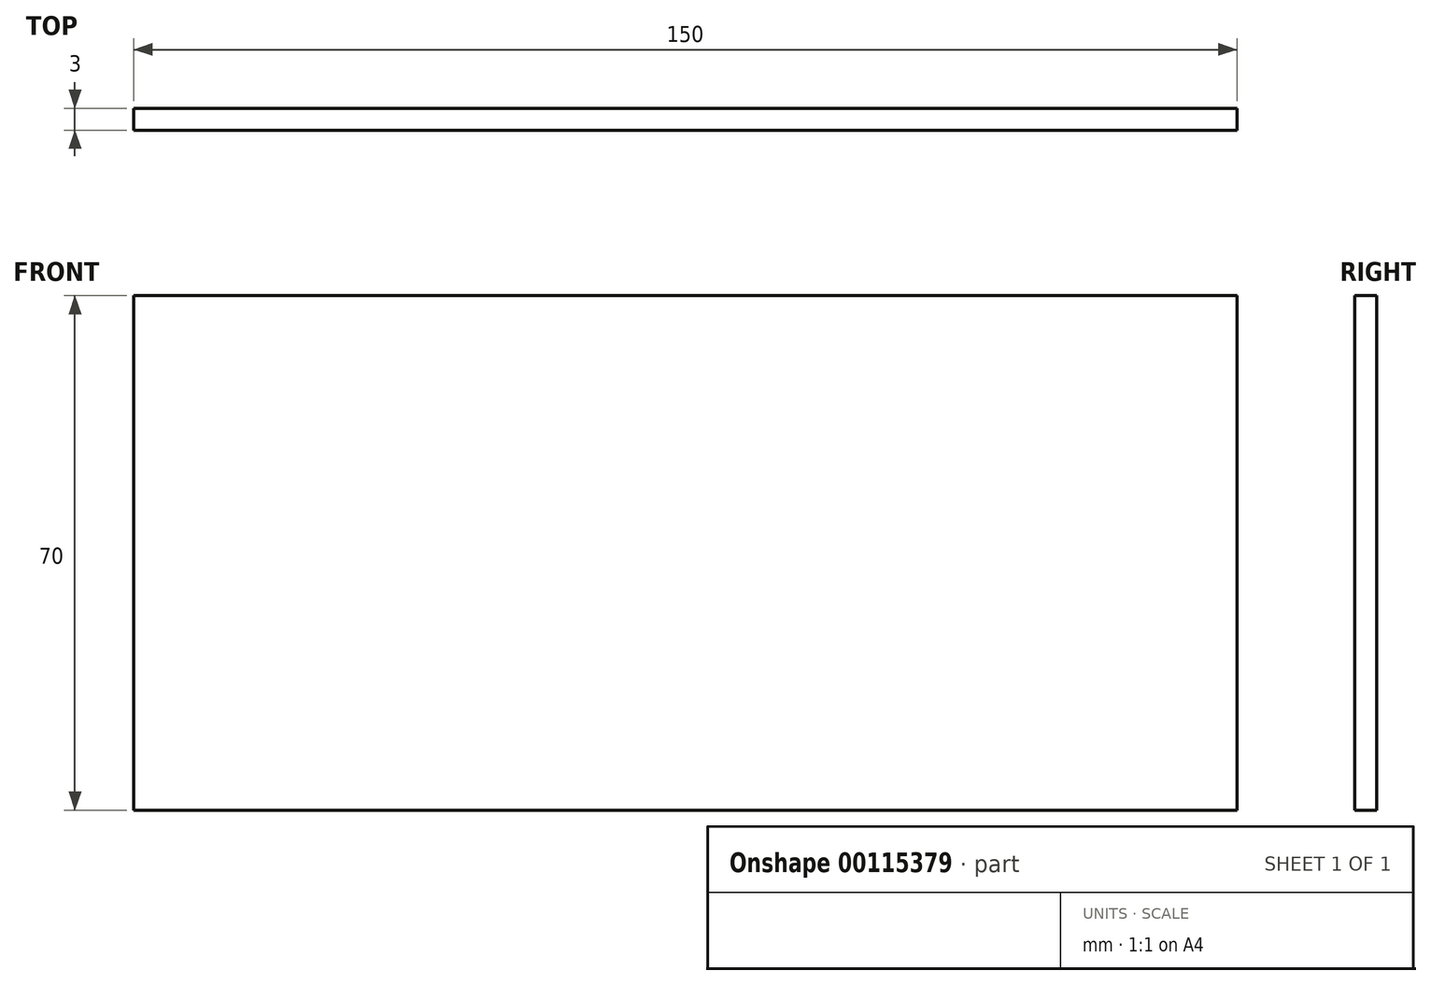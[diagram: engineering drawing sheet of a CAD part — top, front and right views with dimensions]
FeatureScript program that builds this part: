
annotation { "Feature Type Name" : "Feature", "Feature Type Description" : "" }
export const myFeature = defineFeature(function(context is Context, id is Id, definition is map)
    precondition{}
    {
        {
            var Q0;
            Q0=qCreatedBy(makeId("Front.planeOp"),FACE);
            var sketch = newSketch(context, id + "F0", { "sketchPlane" : qUnion([Q0])});
            skLineSegment(sketch, "E0.bottom", {"start": v(0, 0) * mm, "end": v(150, 0) * mm});
            skLineSegment(sketch, "E0.top", {"start": v(0, 70) * mm, "end": v(150, 70) * mm});
            skLineSegment(sketch, "E0.left", {"start": v(0, 0) * mm, "end": v(0, 70) * mm});
            skLineSegment(sketch, "E0.right", {"start": v(150, 0) * mm, "end": v(150, 70) * mm});
            skSolve(sketch);
        }
        {
            var Q0;
            Q0=makeQuery(id+"F0.imprint","IMPRINT",FACE,{"disambiguationData":[TD([[makeQuery(id+"F0.imprint","IMPRINT",EDGE,{"derivedFrom":sQuery(id+"F0.wireOp",EDGE,"E0.bottom")}),1.0]])]});
            extrude(context, id + "F1", {"entities" : qUnion([Q0]), "depth" : 3 * mm});
        }
        {
            var Q0;
            Q0=makeQuery(id+"F1.opExtrude","CAP_FACE",FACE,{"disambiguationData":[OSD([sQuery(id+"F0.wireOp",EDGE,"E0.bottom"),sQuery(id+"F0.wireOp",EDGE,"E0.top"),sQuery(id+"F0.wireOp",EDGE,"E0.left"),sQuery(id+"F0.wireOp",EDGE,"E0.right")])],"isStart":false});
            var sketch = newSketch(context, id + "F2", { "sketchPlane" : qUnion([Q0])});
            skCircle(sketch, "E1", {"center": v(35, 35) * mm, "radius": 22.5 * mm});
            skSolve(sketch);
        }
        {
            var Q0;
            Q0=makeQuery(id+"F2.imprint","IMPRINT",FACE,{"disambiguationData":[TD([[makeQuery(id+"F2.imprint","IMPRINT",EDGE,{"derivedFrom":sQuery(id+"F2.wireOp",EDGE,"E1")}),1.0]])]});
            extrude(context, id + "F3", {"entities" : qUnion([Q0]), "operationType" : NewBodyOperationType.REMOVE, "depth" : 5 * mm});
        }
    });
